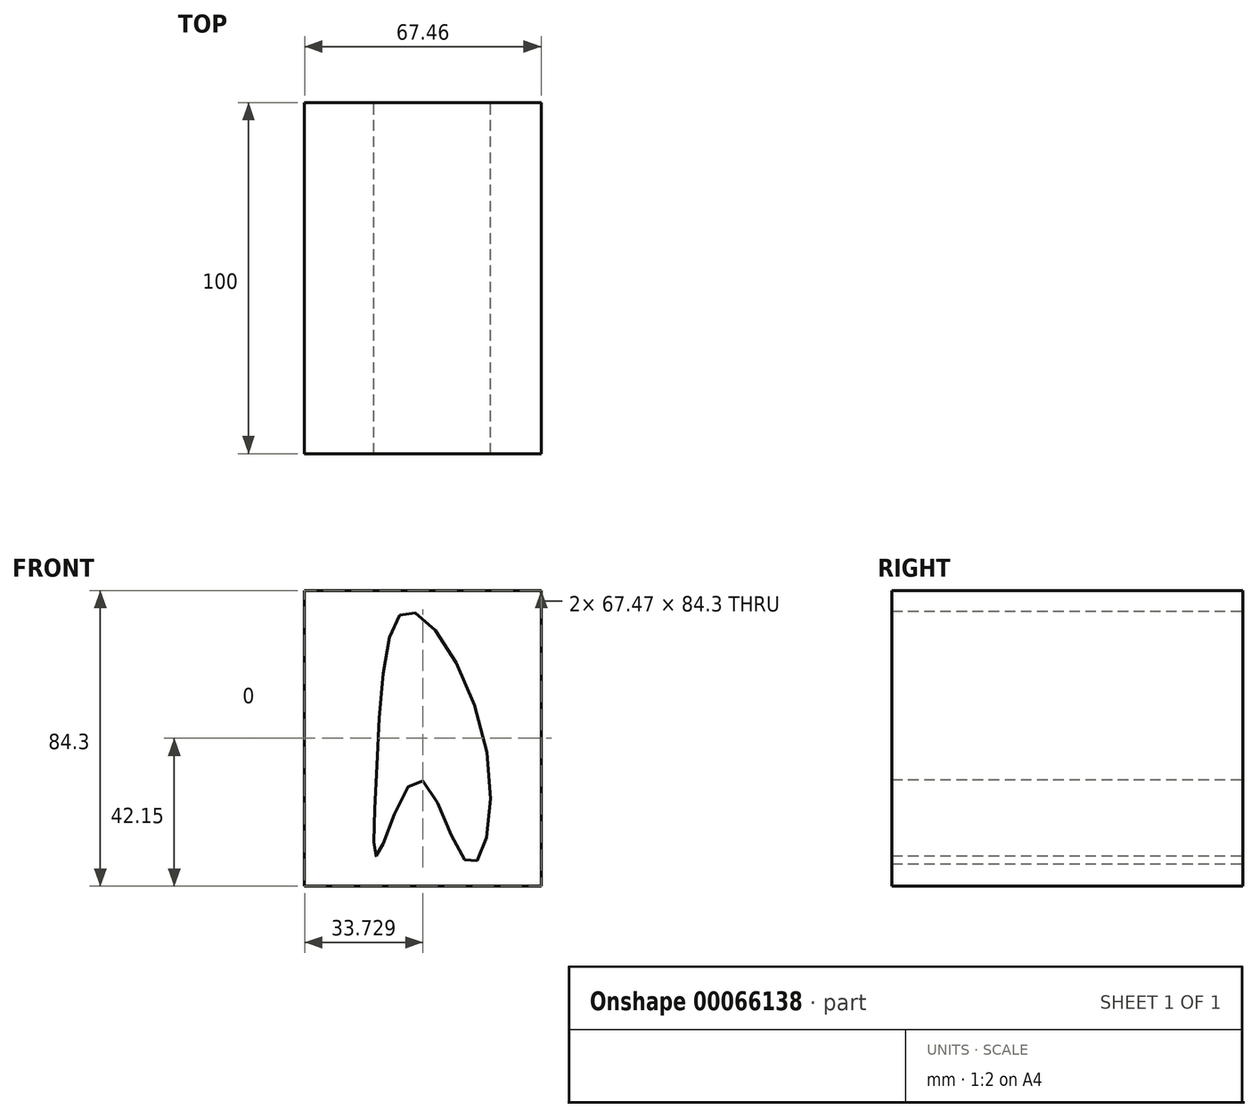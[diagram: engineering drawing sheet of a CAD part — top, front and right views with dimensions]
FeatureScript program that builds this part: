
annotation { "Feature Type Name" : "Feature", "Feature Type Description" : "" }
export const myFeature = defineFeature(function(context is Context, id is Id, definition is map)
    precondition{}
    {
        {
            var Q0;
            Q0=qCreatedBy(makeId("Front.planeOp"),FACE);
            var sketch = newSketch(context, id + "F0", { "sketchPlane" : qUnion([Q0])});
            skFitSpline(sketch, "E0", {"points": [v(-40.97, -7.66) * mm, v(-40.6, -33.08) * mm, v(-29.18, -11.72) * mm, v(-15.19, -35.3) * mm, v(-9.3, -5.45) * mm, v(-32.5, 36.17) * mm, v(-40.97, -7.66) * mm]});
            skLineSegment(sketch, "E1.rect.bottom", {"start": v(5.9, -42.15) * mm, "end": v(-61.56, -42.15) * mm});
            skLineSegment(sketch, "E1.rect.top", {"start": v(5.9, 42.15) * mm, "end": v(-61.56, 42.15) * mm});
            skLineSegment(sketch, "E1.rect.left", {"start": v(5.9, -42.15) * mm, "end": v(5.9, 42.15) * mm});
            skLineSegment(sketch, "E1.rect.right", {"start": v(-61.56, -42.15) * mm, "end": v(-61.56, 42.15) * mm});
            skPoint(sketch, "E1.rect.middle", {"position": v(-27.83, 0) * mm});
            skSolve(sketch);
        }
        {
            var Q0;
            Q0 = qSketchRegion(id + "F0", true);
            extrude(context, id + "F1", {"entities" : qUnion([Q0]), "depth" : 100 * mm});
        }
    });
